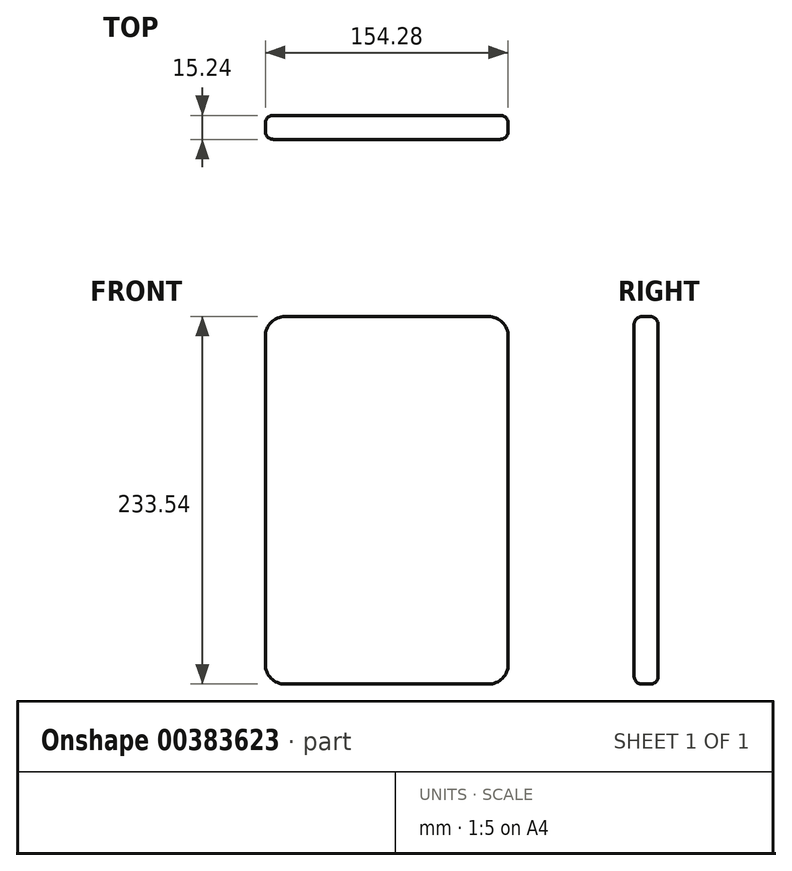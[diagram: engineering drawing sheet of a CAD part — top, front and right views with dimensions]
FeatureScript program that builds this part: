
annotation { "Feature Type Name" : "Feature", "Feature Type Description" : "" }
export const myFeature = defineFeature(function(context is Context, id is Id, definition is map)
    precondition{}
    {
        {
            var Q0;
            Q0=qCreatedBy(makeId("Front.planeOp"),FACE);
            var sketch = newSketch(context, id + "F0", { "sketchPlane" : qUnion([Q0])});
            skLineSegment(sketch, "E0.bottom", {"start": v(77.14, 116.77) * mm, "end": v(-77.14, 116.77) * mm});
            skLineSegment(sketch, "E0.top", {"start": v(77.14, -116.77) * mm, "end": v(-77.14, -116.77) * mm});
            skLineSegment(sketch, "E0.left", {"start": v(77.14, 116.77) * mm, "end": v(77.14, -116.77) * mm});
            skLineSegment(sketch, "E0.right", {"start": v(-77.14, 116.77) * mm, "end": v(-77.14, -116.77) * mm});
            skPoint(sketch, "E0.middle", {"position": v(0, 0) * mm});
            skSolve(sketch);
        }
        {
            var Q0;
            Q0=qCreatedBy(makeId("Top.planeOp"),FACE);
            var sketch = newSketch(context, id + "F1", { "sketchPlane" : qUnion([Q0])});
            skLineSegment(sketch, "E1.bottom", {"start": v(77.5, 12.72) * mm, "end": v(-77.5, 12.72) * mm});
            skLineSegment(sketch, "E1.top", {"start": v(77.5, -12.72) * mm, "end": v(-77.5, -12.72) * mm});
            skLineSegment(sketch, "E1.left", {"start": v(77.5, 12.72) * mm, "end": v(77.5, -12.72) * mm});
            skLineSegment(sketch, "E1.right", {"start": v(-77.5, 12.72) * mm, "end": v(-77.5, -12.72) * mm});
            skPoint(sketch, "E1.middle", {"position": v(0, 0) * mm});
            skSolve(sketch);
        }
        {
            var Q0;
            Q0=makeQuery(id+"F0.imprint","IMPRINT",FACE,{"disambiguationData":[TD([[makeQuery(id+"F0.imprint","IMPRINT",EDGE,{"derivedFrom":sQuery(id+"F0.wireOp",EDGE,"E0.bottom")}),1.0]])]});
            extrude(context, id + "F2", {"entities" : qUnion([Q0]), "oppositeDirection" : true, "depth" : 15.24 * mm});
        }
        {
            var Q0;
            Q0=makeQuery(id+"F2.opExtrude","CAP_FACE",FACE,{"disambiguationData":[OSD([sQuery(id+"F0.wireOp",EDGE,"E0.bottom"),sQuery(id+"F0.wireOp",EDGE,"E0.top"),sQuery(id+"F0.wireOp",EDGE,"E0.left"),sQuery(id+"F0.wireOp",EDGE,"E0.right")])],"isStart":false});
            extrude(context, id + "F3", {"entities" : qUnion([Q0]), "operationType" : NewBodyOperationType.ADD, "oppositeDirection" : true, "depth" : 15.24 * mm});
        }
        {
            var Q0;
            Q0=makeQuery(id+"F2.opExtrude","SWEPT_EDGE",EDGE,{"disambiguationData":[OSD([sQuery(id+"F0.wireOp",EDGE,"E0.bottom"),sQuery(id+"F0.wireOp",EDGE,"E0.left")])]});
            fillet(context, id + "F4", {"entities" : qUnion([Q0]), "radius" : 12.7 * mm, "tangentPropagation" : true, "allowEdgeOverflow" : false});
        }
        {
            var Q0;
            Q0=sQuery(id+"F1.wireOp",EDGE,"E1.left");
            extrude(context, id + "F5", {"bodyType" : ToolBodyType.SURFACE, "surfaceEntities" : qUnion([Q0]), "depth" : 25.4 * mm});
        }
        {
            var Q0;
            Q0=makeQuery(id+"F2.opExtrude","SWEPT_EDGE",EDGE,{"disambiguationData":[OSD([sQuery(id+"F0.wireOp",EDGE,"E0.bottom"),sQuery(id+"F0.wireOp",EDGE,"E0.right")])]});
            fillet(context, id + "F6", {"entities" : qUnion([Q0]), "radius" : 12.7 * mm, "tangentPropagation" : true, "allowEdgeOverflow" : false});
        }
        {
            var Q0;
            Q0=makeQuery(id+"F2.opExtrude","SWEPT_EDGE",EDGE,{"disambiguationData":[OSD([sQuery(id+"F0.wireOp",EDGE,"E0.top"),sQuery(id+"F0.wireOp",EDGE,"E0.left")])]});
            fillet(context, id + "F7", {"entities" : qUnion([Q0]), "radius" : 12.7 * mm, "tangentPropagation" : true, "allowEdgeOverflow" : false});
        }
        {
            var Q0;
            Q0=makeQuery(id+"F2.opExtrude","SWEPT_EDGE",EDGE,{"disambiguationData":[OSD([sQuery(id+"F0.wireOp",EDGE,"E0.top"),sQuery(id+"F0.wireOp",EDGE,"E0.right")])]});
            fillet(context, id + "F8", {"entities" : qUnion([Q0]), "radius" : 12.7 * mm, "tangentPropagation" : true, "allowEdgeOverflow" : false});
        }
        {
            var Q0;
            Q0=makeQuery(id+"F2.opExtrude","CAP_EDGE",EDGE,{"disambiguationData":[OSD([sQuery(id+"F0.wireOp",EDGE,"E0.right")])],"isStart":false});
            var Q1;
            Q1=makeQuery(id+"F2.opExtrude","CAP_EDGE",EDGE,{"disambiguationData":[OSD([sQuery(id+"F0.wireOp",EDGE,"E0.right")])],"isStart":true});
            var Q2;
            Q2=makeQuery(id+"F2.opExtrude","CAP_EDGE",EDGE,{"disambiguationData":[OSD([sQuery(id+"F0.wireOp",EDGE,"E0.left")])],"isStart":true});
            var Q3;
            Q3=makeQuery(id+"F2.opExtrude","CAP_EDGE",EDGE,{"disambiguationData":[OSD([sQuery(id+"F0.wireOp",EDGE,"E0.left")])],"isStart":false});
            var Q4;
            Q4=makeQuery(id+"F2.opExtrude","CAP_EDGE",EDGE,{"disambiguationData":[OSD([sQuery(id+"F0.wireOp",EDGE,"E0.bottom")])],"isStart":true});
            var Q5;
            Q5=makeQuery(id+"F2.opExtrude","CAP_EDGE",EDGE,{"disambiguationData":[OSD([sQuery(id+"F0.wireOp",EDGE,"E0.bottom")])],"isStart":false});
            var Q6;
            Q6=makeQuery(id+"F2.opExtrude","CAP_EDGE",EDGE,{"disambiguationData":[OSD([sQuery(id+"F0.wireOp",EDGE,"E0.top")])],"isStart":false});
            var Q7;
            Q7=makeQuery(id+"F2.opExtrude","CAP_EDGE",EDGE,{"disambiguationData":[OSD([sQuery(id+"F0.wireOp",EDGE,"E0.top")])],"isStart":true});
            fillet(context, id + "F9", {"entities" : qUnion([Q0, Q1, Q2, Q3, Q4, Q5, Q6, Q7]), "radius" : 5.08 * mm, "tangentPropagation" : true, "allowEdgeOverflow" : false});
        }
    });
